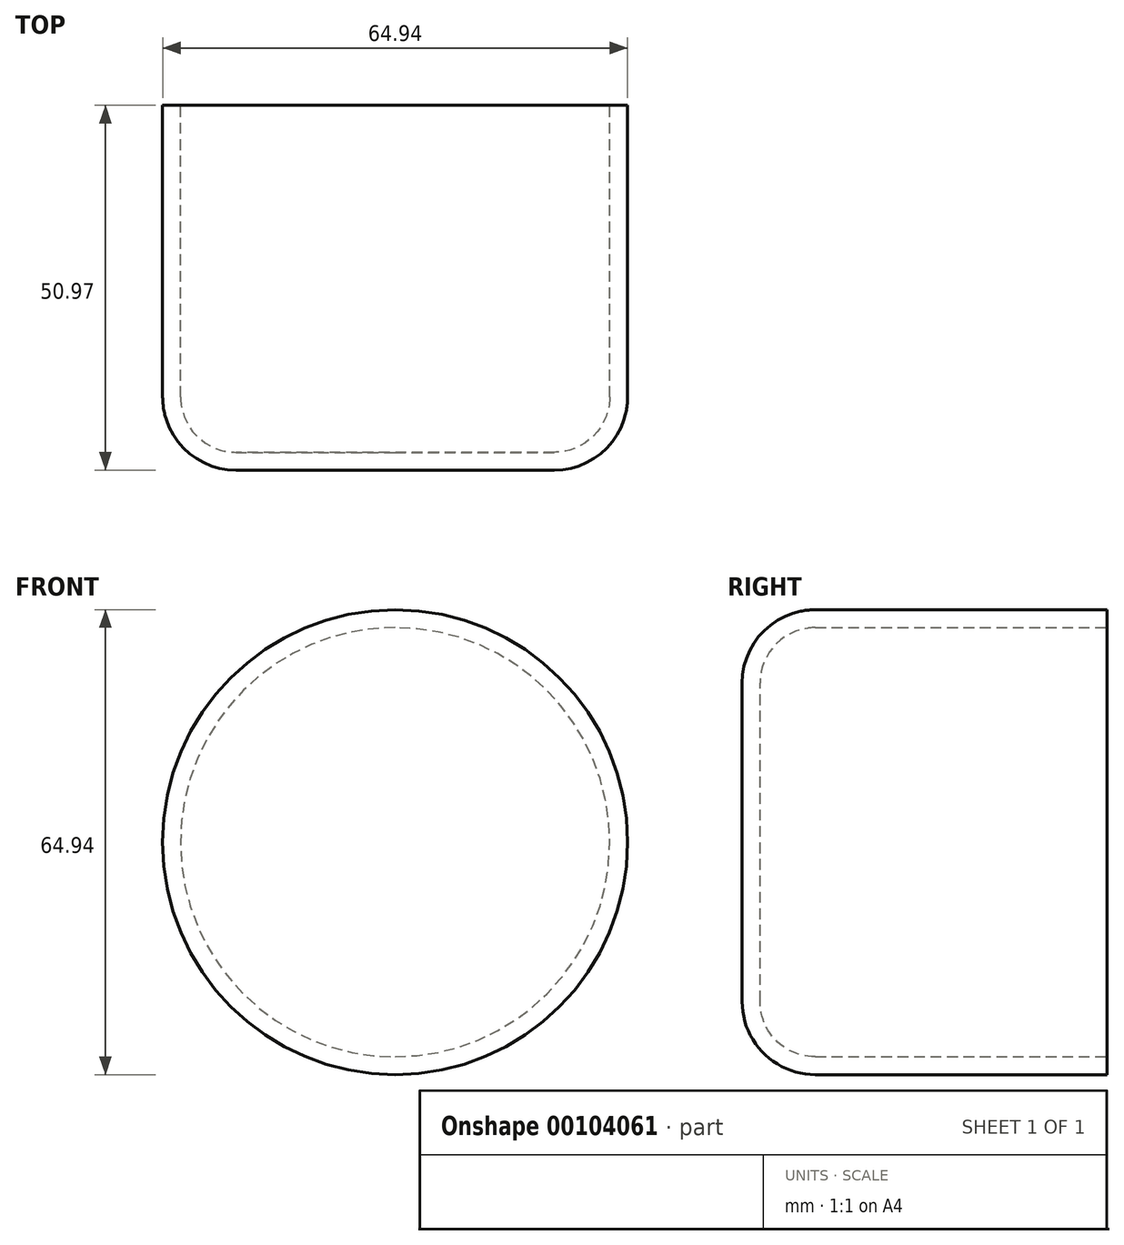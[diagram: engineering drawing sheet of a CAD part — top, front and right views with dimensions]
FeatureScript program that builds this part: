
annotation { "Feature Type Name" : "Feature", "Feature Type Description" : "" }
export const myFeature = defineFeature(function(context is Context, id is Id, definition is map)
    precondition{}
    {
        {
            var Q0;
            Q0=qCreatedBy(makeId("Front.planeOp"),FACE);
            var sketch = newSketch(context, id + "F0", { "sketchPlane" : qUnion([Q0])});
            skCircle(sketch, "E0", {"center": v(0, 0) * mm, "radius": 32.47 * mm});
            skSolve(sketch);
        }
        {
            var Q0;
            Q0 = qSketchRegion(id + "F0", true);
            extrude(context, id + "F1", {"entities" : qUnion([Q0]), "depth" : 18.48 * mm, "hasSecondDirection" : true, "secondDirectionOppositeDirection" : true, "secondDirectionDepth" : 25 * mm});
        }
        {
            var Q0;
            Q0=makeQuery(id+"F1.opExtrude","CAP_EDGE",EDGE,{"disambiguationData":[OSD([sQuery(id+"F0.wireOp",EDGE,"E0")])],"isStart":false});
            fillet(context, id + "F2", {"entities" : qUnion([Q0]), "radius" : 10.22 * mm, "tangentPropagation" : true, "allowEdgeOverflow" : false});
        }
        {
            var Q0;
            Q0=makeQuery(id+"F1.opExtrude","CAP_FACE",FACE,{"disambiguationData":[OSD([sQuery(id+"F0.wireOp",EDGE,"E0")])],"isStart":true});
            shell(context, id + "F3", {"entities" : qUnion([Q0]), "thickness" : 2.5 * mm});
        }
        {
            var Q0;
            Q0=makeQuery(id+"F1.opExtrude","SWEPT_BODY",BODY,{"disambiguationData":[OSD([sQuery(id+"F0.wireOp",EDGE,"E0")])]});
            var Q1;
            {var subQ0=sQuery(id+"F0.wireOp",EDGE,"E0");Q1=makeQuery(id+"F3.opShell","OFFSET_FACE",FACE,{"disambiguationData":[OSD([subQ0]),TDD([makeQuery(id+"F1.opExtrude","SWEPT_FACE",FACE,{"disambiguationData":[OSD([subQ0])]})])]});}
            transform(context, id + "F4", {"entities" : qUnion([Q0]), "transformType" : TransformType.TRANSLATION_DISTANCE, "transformDirection" : qUnion([Q1]), "distance" : 25 * mm, "makeCopy" : false});
        }
        {
            var Q0;
            Q0=makeQuery(id+"F1.opExtrude","CAP_FACE",FACE,{"disambiguationData":[OSD([sQuery(id+"F0.wireOp",EDGE,"E0")])],"isStart":true});
            extrude(context, id + "F5", {"entities" : qUnion([Q0]), "operationType" : NewBodyOperationType.ADD, "depth" : 7.5 * mm});
        }
    });
